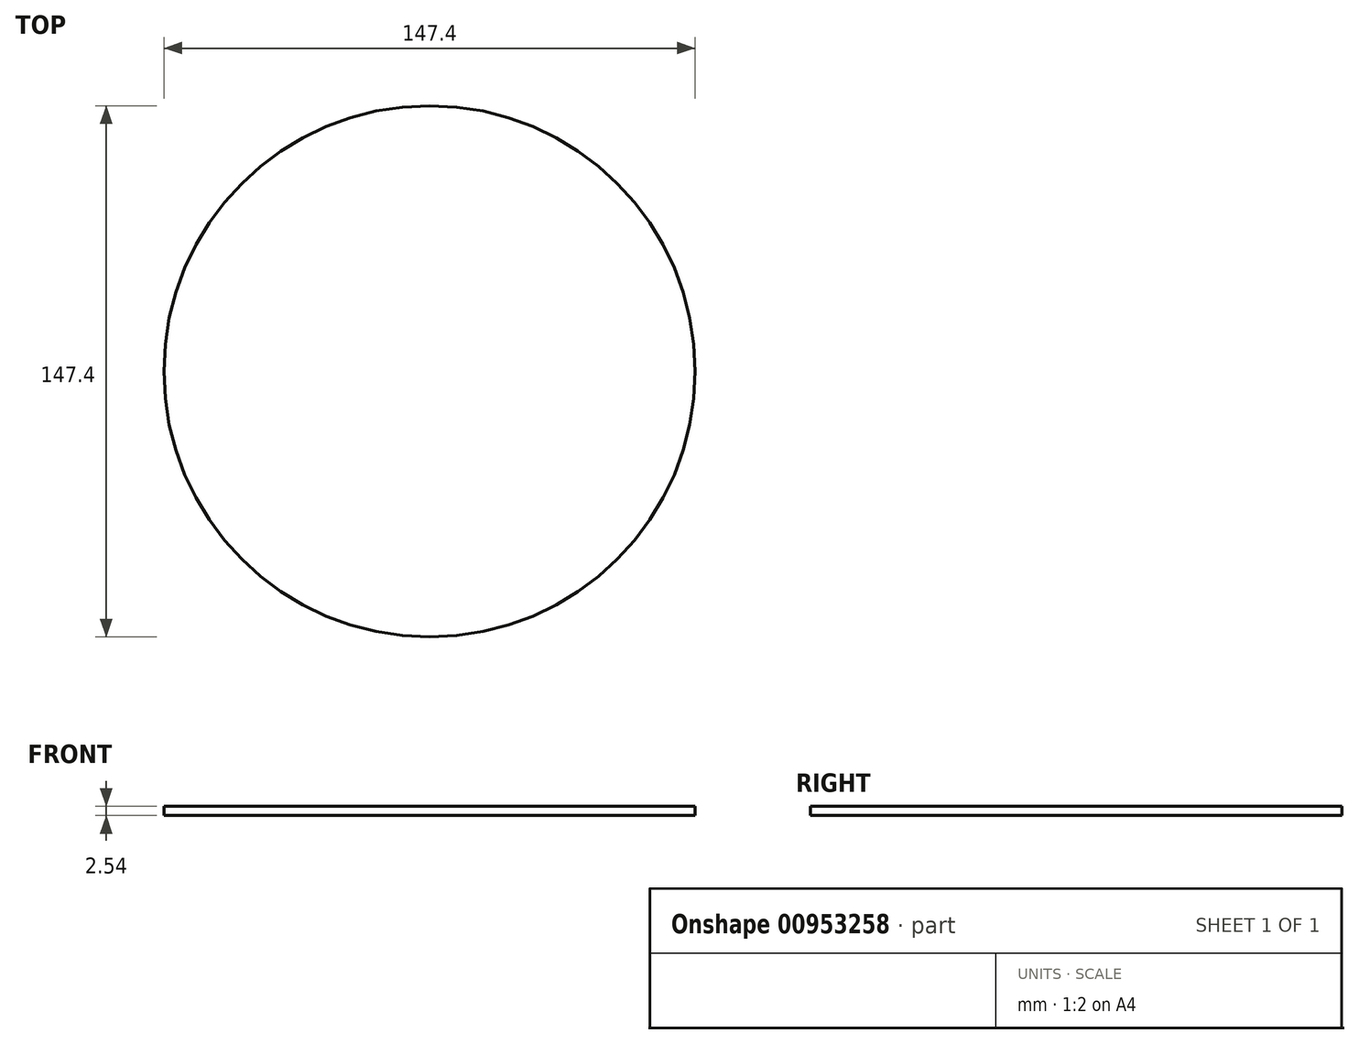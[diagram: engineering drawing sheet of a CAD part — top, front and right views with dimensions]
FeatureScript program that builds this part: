
annotation { "Feature Type Name" : "Feature", "Feature Type Description" : "" }
export const myFeature = defineFeature(function(context is Context, id is Id, definition is map)
    precondition{}
    {
        {
            var Q0;
            Q0=qCreatedBy(makeId("Top.planeOp"),FACE);
            var sketch = newSketch(context, id + "F0", { "sketchPlane" : qUnion([Q0])});
            skCircle(sketch, "E0", {"center": v(0, 0) * mm, "radius": 73.7 * mm});
            skSolve(sketch);
        }
        {
            var Q0;
            Q0=makeQuery(id+"F0.imprint","IMPRINT",FACE,{"disambiguationData":[TD([[makeQuery(id+"F0.imprint","IMPRINT",EDGE,{"derivedFrom":sQuery(id+"F0.wireOp",EDGE,"E0")}),1.0]])]});
            extrude(context, id + "F1", {"entities" : qUnion([Q0]), "depth" : 2.54 * mm, "offsetDistance" : 25.4 * mm});
        }
    });
